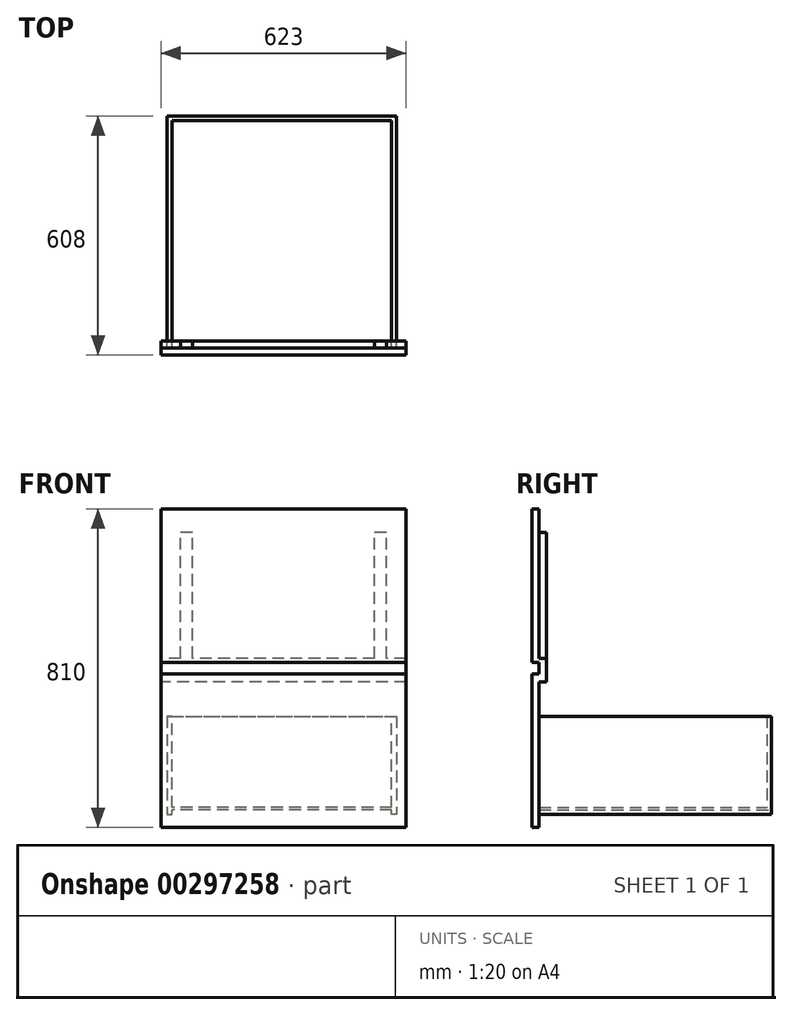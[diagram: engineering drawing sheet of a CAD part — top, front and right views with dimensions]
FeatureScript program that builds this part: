
annotation { "Feature Type Name" : "Feature", "Feature Type Description" : "" }
export const myFeature = defineFeature(function(context is Context, id is Id, definition is map)
    precondition{}
    {
        {
            var Q0;
            Q0=qCreatedBy(makeId("Front.planeOp"),FACE);
            var sketch = newSketch(context, id + "F0", { "sketchPlane" : qUnion([Q0])});
            skLineSegment(sketch, "E0.bottom", {"start": v(279, -3) * mm, "end": v(-279, -3) * mm});
            skLineSegment(sketch, "E0.top", {"start": v(279, 3) * mm, "end": v(-279, 3) * mm});
            skPoint(sketch, "E0.middle", {"position": v(0, 0) * mm});
            skLineSegment(sketch, "E1", {"start": v(-279, 3) * mm, "end": v(-279, 235) * mm});
            skLineSegment(sketch, "E2", {"start": v(-279, 235) * mm, "end": v(-291, 235) * mm});
            skLineSegment(sketch, "E3", {"start": v(-291, 235) * mm, "end": v(-291, -15) * mm});
            skLineSegment(sketch, "E4", {"start": v(-291, -15) * mm, "end": v(-279, -15) * mm});
            skLineSegment(sketch, "E5", {"start": v(-279, -15) * mm, "end": v(-279, -3) * mm});
            skLineSegment(sketch, "E6", {"start": v(279, 3) * mm, "end": v(279, 235) * mm});
            skLineSegment(sketch, "E7", {"start": v(279, 235) * mm, "end": v(291, 235) * mm});
            skLineSegment(sketch, "E8", {"start": v(291, 235) * mm, "end": v(291, -15) * mm});
            skLineSegment(sketch, "E9", {"start": v(291, -15) * mm, "end": v(279, -15) * mm});
            skLineSegment(sketch, "E10", {"start": v(279, -15) * mm, "end": v(279, -3) * mm});
            skSolve(sketch);
        }
        {
            var Q0;
            Q0=qSketchRegion(id+"F0",true);
            extrude(context, id + "F1", {"entities" : qUnion([Q0]), "depth" : 590 * mm});
        }
        {
            var Q0;
            Q0=makeQuery(id+"F1.opExtrude","SWEPT_FACE",FACE,{"disambiguationData":[OSD([sQuery(id+"F0.wireOp",EDGE,"E6")])]});
            var sketch = newSketch(context, id + "F2", { "sketchPlane" : qUnion([Q0])});
            skLineSegment(sketch, "E11.bottom", {"start": v(0, 235) * mm, "end": v(12, 235) * mm});
            skLineSegment(sketch, "E11.top", {"start": v(0, 3) * mm, "end": v(12, 3) * mm});
            skLineSegment(sketch, "E11.left", {"start": v(0, 235) * mm, "end": v(0, 3) * mm});
            skLineSegment(sketch, "E11.right", {"start": v(12, 235) * mm, "end": v(12, 3) * mm});
            skSolve(sketch);
        }
        {
            var Q0;
            Q0=qSketchRegion(id+"F2",true);
            extrude(context, id + "F3", {"entities" : qUnion([Q0]), "operationType" : NewBodyOperationType.ADD, "depth" : 558 * mm});
        }
        {
            var Q0;
            Q0=makeQuery(id+"F1.opExtrude","CAP_FACE",FACE,{"disambiguationData":[OSD([sQuery(id+"F0.wireOp",EDGE,"E0.bottom"),sQuery(id+"F0.wireOp",EDGE,"E0.top"),sQuery(id+"F0.wireOp",EDGE,"E1"),sQuery(id+"F0.wireOp",EDGE,"E2"),sQuery(id+"F0.wireOp",EDGE,"E3"),sQuery(id+"F0.wireOp",EDGE,"E4"),sQuery(id+"F0.wireOp",EDGE,"E5"),sQuery(id+"F0.wireOp",EDGE,"E6"),sQuery(id+"F0.wireOp",EDGE,"E7"),sQuery(id+"F0.wireOp",EDGE,"E8"),sQuery(id+"F0.wireOp",EDGE,"E9"),sQuery(id+"F0.wireOp",EDGE,"E10")])],"isStart":false});
            var sketch = newSketch(context, id + "F4", { "sketchPlane" : qUnion([Q0])});
            skLineSegment(sketch, "E12.bottom", {"start": v(-307, 342) * mm, "end": v(316, 342) * mm});
            skLineSegment(sketch, "E12.top", {"start": v(-307, -48) * mm, "end": v(316, -48) * mm});
            skLineSegment(sketch, "E12.left", {"start": v(-307, 342) * mm, "end": v(-307, -48) * mm});
            skLineSegment(sketch, "E12.right", {"start": v(316, 342) * mm, "end": v(316, -48) * mm});
            skSolve(sketch);
        }
        {
            var Q0;
            Q0=qSketchRegion(id+"F4",true);
            extrude(context, id + "F5", {"entities" : qUnion([Q0]), "operationType" : NewBodyOperationType.ADD, "depth" : 18 * mm});
        }
        {
            var Q0;
            Q0=makeQuery(id+"F5.opExtrude","CAP_FACE",FACE,{"disambiguationData":[OSD([sQuery(id+"F4.wireOp",EDGE,"E12.bottom"),sQuery(id+"F4.wireOp",EDGE,"E12.top"),sQuery(id+"F4.wireOp",EDGE,"E12.left"),sQuery(id+"F4.wireOp",EDGE,"E12.right")])],"isStart":true});
            var sketch = newSketch(context, id + "F6", { "sketchPlane" : qUnion([Q0])});
            skLineSegment(sketch, "E13.bottom", {"start": v(-316, 322) * mm, "end": v(307, 322) * mm});
            skLineSegment(sketch, "E13.top", {"start": v(-316, 382) * mm, "end": v(307, 382) * mm});
            skLineSegment(sketch, "E13.left", {"start": v(-316, 322) * mm, "end": v(-316, 382) * mm});
            skLineSegment(sketch, "E13.right", {"start": v(307, 322) * mm, "end": v(307, 382) * mm});
            skSolve(sketch);
        }
        {
            var Q0;
            Q0 = qSketchRegion(id + "F6", true);
            extrude(context, id + "F7", {"entities" : qUnion([Q0]), "operationType" : NewBodyOperationType.ADD, "depth" : 18 * mm});
        }
        {
            var Q0;
            Q0=makeQuery(id+"F7.opExtrude","CAP_FACE",FACE,{"disambiguationData":[OSD([sQuery(id+"F6.wireOp",EDGE,"E13.bottom"),sQuery(id+"F6.wireOp",EDGE,"E13.top"),sQuery(id+"F6.wireOp",EDGE,"E13.left"),sQuery(id+"F6.wireOp",EDGE,"E13.right")])],"isStart":true});
            var sketch = newSketch(context, id + "F8", { "sketchPlane" : qUnion([Q0])});
            skLineSegment(sketch, "E14.bottom", {"start": v(-307, 372) * mm, "end": v(316, 372) * mm});
            skLineSegment(sketch, "E14.top", {"start": v(-307, 762) * mm, "end": v(316, 762) * mm});
            skLineSegment(sketch, "E14.left", {"start": v(-307, 372) * mm, "end": v(-307, 762) * mm});
            skLineSegment(sketch, "E14.right", {"start": v(316, 372) * mm, "end": v(316, 762) * mm});
            skSolve(sketch);
        }
        {
            var Q0;
            Q0 = qSketchRegion(id + "F8", true);
            extrude(context, id + "F9", {"entities" : qUnion([Q0]), "operationType" : NewBodyOperationType.ADD, "depth" : 18 * mm});
        }
        {
            var Q0;
            Q0=makeQuery(id+"F9.opExtrude","CAP_FACE",FACE,{"disambiguationData":[OSD([sQuery(id+"F8.wireOp",EDGE,"E14.bottom"),sQuery(id+"F8.wireOp",EDGE,"E14.top"),sQuery(id+"F8.wireOp",EDGE,"E14.left"),sQuery(id+"F8.wireOp",EDGE,"E14.right")])],"isStart":true});
            var sketch = newSketch(context, id + "F10", { "sketchPlane" : qUnion([Q0])});
            skLineSegment(sketch, "E15.bottom", {"start": v(-266, 382) * mm, "end": v(-236, 382) * mm});
            skLineSegment(sketch, "E15.top", {"start": v(-266, 702) * mm, "end": v(-236, 702) * mm});
            skLineSegment(sketch, "E15.left", {"start": v(-266, 382) * mm, "end": v(-266, 702) * mm});
            skLineSegment(sketch, "E15.right", {"start": v(-236, 382) * mm, "end": v(-236, 702) * mm});
            skLineSegment(sketch, "E16.bottom", {"start": v(227, 382) * mm, "end": v(257, 382) * mm});
            skLineSegment(sketch, "E16.top", {"start": v(227, 702) * mm, "end": v(257, 702) * mm});
            skLineSegment(sketch, "E16.left", {"start": v(227, 382) * mm, "end": v(227, 702) * mm});
            skLineSegment(sketch, "E16.right", {"start": v(257, 382) * mm, "end": v(257, 702) * mm});
            skSolve(sketch);
        }
        {
            var Q0;
            Q0 = qSketchRegion(id + "F10", true);
            extrude(context, id + "F11", {"entities" : qUnion([Q0]), "operationType" : NewBodyOperationType.ADD, "depth" : 18 * mm});
        }
    });
